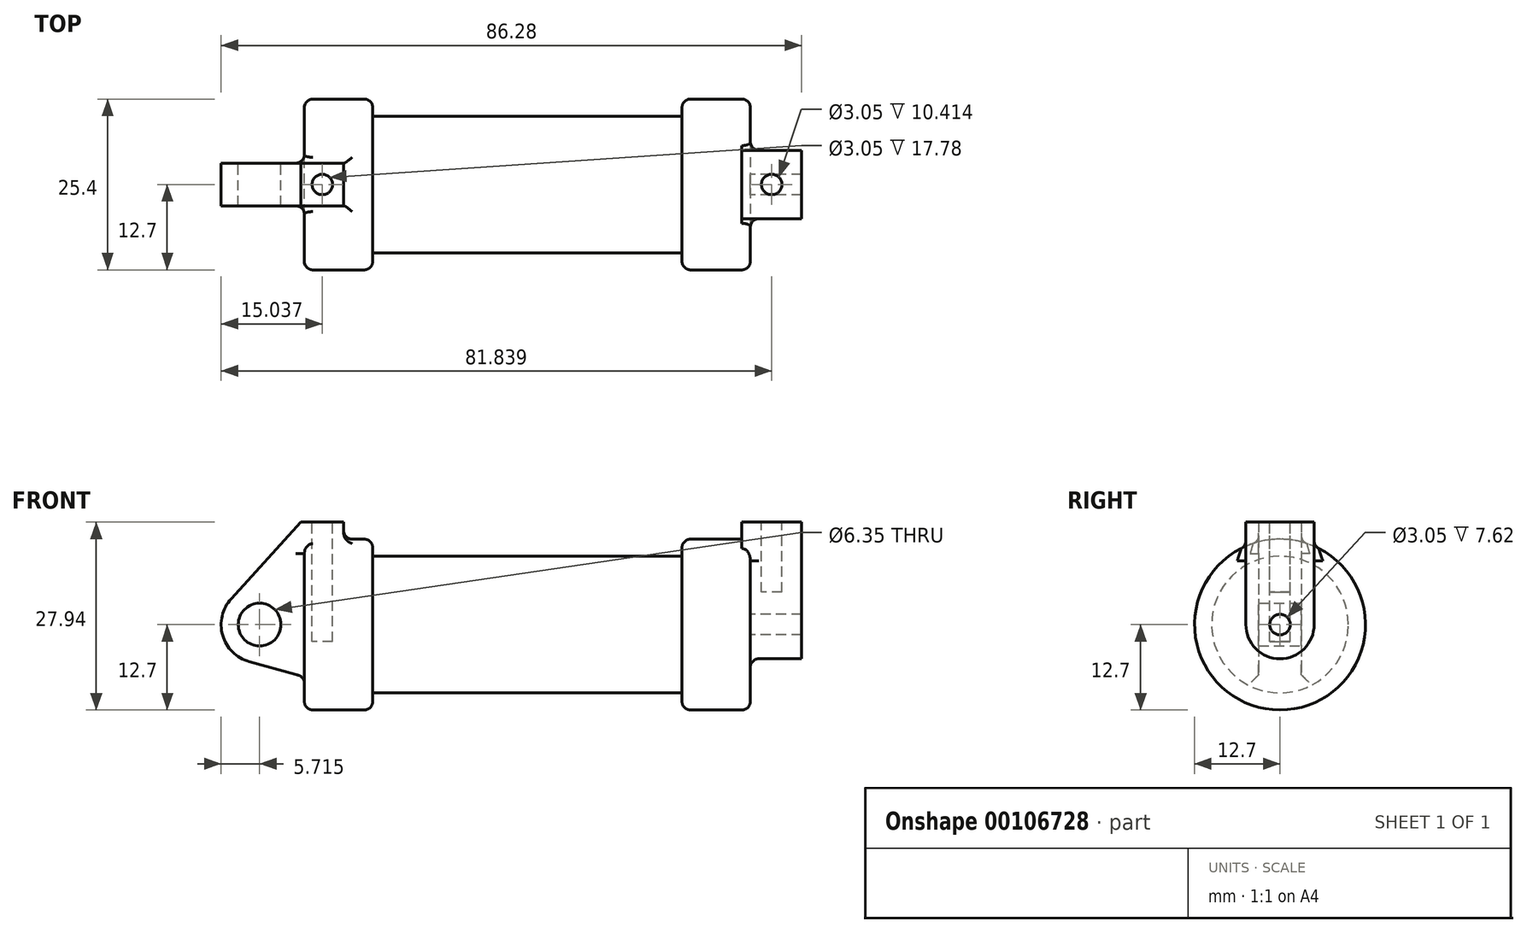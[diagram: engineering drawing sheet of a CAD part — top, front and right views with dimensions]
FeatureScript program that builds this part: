
annotation { "Feature Type Name" : "Feature", "Feature Type Description" : "" }
export const myFeature = defineFeature(function(context is Context, id is Id, definition is map)
    precondition{}
    {
        {
            var Q0;
            Q0=qCreatedBy(makeId("Front.planeOp"),FACE);
            var sketch = newSketch(context, id + "F0", { "sketchPlane" : qUnion([Q0])});
            skLineSegment(sketch, "E0", {"start": v(0, 0) * mm, "end": v(0, 12.7) * mm});
            skLineSegment(sketch, "E1", {"start": v(0, 12.7) * mm, "end": v(10.16, 12.7) * mm});
            skLineSegment(sketch, "E2", {"start": v(10.16, 12.7) * mm, "end": v(10.16, 10.16) * mm});
            skLineSegment(sketch, "E3", {"start": v(10.16, 10.16) * mm, "end": v(56.13, 10.16) * mm});
            skLineSegment(sketch, "E4", {"start": v(56.13, 10.16) * mm, "end": v(56.13, 12.7) * mm});
            skLineSegment(sketch, "E5", {"start": v(56.13, 12.7) * mm, "end": v(66.3, 12.7) * mm});
            skLineSegment(sketch, "E6", {"start": v(66.3, 12.7) * mm, "end": v(66.3, 0) * mm});
            skLineSegment(sketch, "E7", {"start": v(66.3, 0) * mm, "end": v(0, 0) * mm});
            skLineSegment(sketch, "E8", {"start": v(5.84, 15.24) * mm, "end": v(-0.5, 15.24) * mm});
            skLineSegment(sketch, "E9", {"start": v(-0.5, 15.24) * mm, "end": v(-10.88, 3.85) * mm});
            skLineSegment(sketch, "E10", {"start": v(0, 0) * mm, "end": v(-6.65, 0) * mm});
            skCircle(sketch, "E11", {"center": v(-6.65, 0) * mm, "radius": 5.72 * mm});
            skCircle(sketch, "E12", {"center": v(-6.65, 0) * mm, "radius": 3.18 * mm});
            skLineSegment(sketch, "E13", {"start": v(5.84, 15.24) * mm, "end": v(5.84, -9.4) * mm});
            skLineSegment(sketch, "E14", {"start": v(5.84, -9.4) * mm, "end": v(-8.18, -5.5) * mm});
            skSolve(sketch);
        }
        {
            var Q0;
            {var subQ0=sQuery(id+"F0.wireOp",EDGE,"E0");Q0=makeQuery(id+"F0.imprint","IMPRINT",FACE,{"disambiguationData":[TD([[makeQuery(id+"F0.imprint","IMPRINT",EDGE,{"derivedFrom":subQ0}),-1.0]])]});}
            var Q1;
            {var subQ0=sQuery(id+"F0.wireOp",EDGE,"E2");Q1=makeQuery(id+"F0.imprint","IMPRINT",FACE,{"disambiguationData":[TD([[makeQuery(id+"F0.imprint","IMPRINT",EDGE,{"derivedFrom":subQ0}),-1.0]])]});}
            var Q2;
            Q2=sQuery(id+"F0.wireOp",EDGE,"E7");
            revolve(context, id + "F1", {"entities" : qUnion([Q0, Q1]), "axis" : qUnion([Q2]), "revolveType" : RevolveType.FULL});
        }
        {
            var Q0;
            {var subQ3=sQuery(id+"F0.wireOp",EDGE,"E0");Q0=makeQuery(id+"F0.imprint","IMPRINT",FACE,{"disambiguationData":[TD([[makeQuery(id+"F0.imprint","IMPRINT",EDGE,{"derivedFrom":subQ3}),1.0]])]});}
            var Q1;
            {var subQ4=sQuery(id+"F0.wireOp",EDGE,"E12");Q1=makeQuery(id+"F0.imprint","IMPRINT",FACE,{"disambiguationData":[TD([[makeQuery(id+"F0.imprint","IMPRINT",EDGE,{"derivedFrom":subQ4}),-1.0]])]});}
            var Q2;
            {var subQ0=sQuery(id+"F0.wireOp",EDGE,"E14");Q2=makeQuery(id+"F0.imprint","IMPRINT",FACE,{"disambiguationData":[TD([[makeQuery(id+"F0.imprint","IMPRINT",EDGE,{"derivedFrom":subQ0}),-1.0]])]});}
            var Q3;
            {var subQ0=sQuery(id+"F0.wireOp",EDGE,"E0");Q3=makeQuery(id+"F0.imprint","IMPRINT",FACE,{"disambiguationData":[TD([[makeQuery(id+"F0.imprint","IMPRINT",EDGE,{"derivedFrom":subQ0}),-1.0]])]});}
            extrude(context, id + "F2", {"entities" : qUnion([Q0, Q1, Q2, Q3]), "operationType" : NewBodyOperationType.ADD, "endBound" : BoundingType.SYMMETRIC, "depth" : 6.35 * mm});
        }
        {
            var Q0;
            Q0=makeQuery(id+"F1.opRevolve","SWEPT_FACE",FACE,{"disambiguationData":[OSD([sQuery(id+"F0.wireOp",EDGE,"E6")])]});
            var sketch = newSketch(context, id + "F3", { "sketchPlane" : qUnion([Q0])});
            skCircle(sketch, "E15", {"center": v(0, 0) * mm, "radius": 1.52 * mm});
            skCircle(sketch, "E16", {"center": v(0, 0) * mm, "radius": 5.08 * mm});
            skLineSegment(sketch, "E17", {"start": v(5.08, 0) * mm, "end": v(5.08, 15.24) * mm});
            skLineSegment(sketch, "E18", {"start": v(-5.08, 0) * mm, "end": v(-5.08, 15.24) * mm});
            skLineSegment(sketch, "E19", {"start": v(-5.08, 15.24) * mm, "end": v(5.08, 15.24) * mm});
            skSolve(sketch);
        }
        {
            var Q0;
            {var subQ0=sQuery(id+"F3.wireOp",EDGE,"E19");Q0=makeQuery(id+"F3.imprint","IMPRINT",FACE,{"disambiguationData":[TD([[makeQuery(id+"F3.imprint","IMPRINT",EDGE,{"derivedFrom":subQ0}),-1.0]])]});}
            var Q1;
            {var subQ0=sQuery(id+"F3.wireOp",EDGE,"E17");var subQ1=sQuery(id+"F3.wireOp",EDGE,"E16");var subQ2=makeQuery(id+"F3.imprint","INTERSECT",VERTEX,{"derivedFrom":[subQ1,subQ0]});Q1=makeQuery(id+"F3.imprint","IMPRINT",FACE,{"disambiguationData":[TD([[makeQuery(id+"F3.imprint","IMPRINT",EDGE,{"disambiguationData":[TD([[subQ2,-1.0]])],"derivedFrom":subQ1}),-1.0]])]});}
            var Q2;
            Q2=makeQuery(id+"F3.imprint","IMPRINT",FACE,{"disambiguationData":[TD([[makeQuery(id+"F3.imprint","IMPRINT",EDGE,{"derivedFrom":sQuery(id+"F3.wireOp",EDGE,"E15")}),-1.0]])]});
            extrude(context, id + "F4", {"entities" : qUnion([Q0, Q1, Q2]), "operationType" : NewBodyOperationType.ADD, "depth" : 7.62 * mm});
        }
        {
            var Q0;
            Q0=makeQuery(id+"F4.opExtrude","CAP_FACE",FACE,{"disambiguationData":[OSD([sQuery(id+"F3.wireOp",EDGE,"E15"),sQuery(id+"F3.wireOp",EDGE,"E16"),sQuery(id+"F3.wireOp",EDGE,"E17"),sQuery(id+"F3.wireOp",EDGE,"E18"),sQuery(id+"F3.wireOp",EDGE,"E19")])],"isStart":true});
            extrude(context, id + "F5", {"entities" : qUnion([Q0]), "operationType" : NewBodyOperationType.ADD, "depth" : 1.27 * mm});
        }
        {
            var Q0;
            Q0=makeQuery(id+"F4.boolean.opBoolean","SPLIT",FACE,{"disambiguationData":[TD([makeQuery(id+"F4.opExtrude","SWEPT_FACE",FACE,{"disambiguationData":[OSD([sQuery(id+"F3.wireOp",EDGE,"E15")])]})])],"derivedFrom":makeQuery(id+"F1.opRevolve","SWEPT_FACE",FACE,{"disambiguationData":[OSD([sQuery(id+"F0.wireOp",EDGE,"E6")])]})});
            var Q1;
            Q1=makeQuery(id+"F1.opRevolve","SWEPT_FACE",FACE,{"disambiguationData":[OSD([sQuery(id+"F0.wireOp",EDGE,"E2")])]});
            extrude(context, id + "F6", {"entities" : qUnion([Q0]), "operationType" : NewBodyOperationType.ADD, "endBound" : BoundingType.UP_TO_SURFACE, "oppositeDirection" : true, "endBoundEntityFace" : qUnion([Q1]), "depth" : 25.4 * mm});
        }
        {
            var Q0;
            {var subQ0=sQuery(id+"F3.wireOp",EDGE,"E19");Q0=makeQuery(id+"F5.boolean.opBoolean","MERGE",FACE,{"derivedFrom":[makeQuery(id+"F4.opExtrude","SWEPT_FACE",FACE,{"disambiguationData":[OSD([subQ0])]}),makeQuery(id+"F5.opExtrude","SWEPT_FACE",FACE,{"disambiguationData":[OSD([subQ0])]})]});}
            var sketch = newSketch(context, id + "F7", { "sketchPlane" : qUnion([Q0])});
            skCircle(sketch, "E20", {"center": v(69.47, 0) * mm, "radius": 1.52 * mm});
            skPoint(sketch, "E20.centerSnap0", {"position": v(69.47, -5.08) * mm});
            skPoint(sketch, "E20.centerSnap1", {"position": v(65.02, 0) * mm});
            skSolve(sketch);
        }
        {
            var Q0;
            Q0=makeQuery(id+"F7.imprint","IMPRINT",FACE,{"disambiguationData":[TD([[makeQuery(id+"F7.imprint","IMPRINT",EDGE,{"derivedFrom":sQuery(id+"F7.wireOp",EDGE,"E20")}),1.0]])]});
            extrude(context, id + "F8", {"entities" : qUnion([Q0]), "operationType" : NewBodyOperationType.REMOVE, "oppositeDirection" : true, "depth" : 10.4 * mm});
        }
        {
            var Q0;
            Q0=makeQuery(id+"F2.opExtrude","SWEPT_FACE",FACE,{"disambiguationData":[OSD([sQuery(id+"F0.wireOp",EDGE,"E8")])]});
            var sketch = newSketch(context, id + "F9", { "sketchPlane" : qUnion([Q0])});
            skCircle(sketch, "E21", {"center": v(2.67, 0) * mm, "radius": 1.52 * mm});
            skPoint(sketch, "E21.centerSnap0", {"position": v(2.67, -3.18) * mm});
            skPoint(sketch, "E21.centerSnap1", {"position": v(-0.5, 0) * mm});
            skSolve(sketch);
        }
        {
            var Q0;
            Q0=makeQuery(id+"F9.imprint","IMPRINT",FACE,{"disambiguationData":[TD([[makeQuery(id+"F9.imprint","IMPRINT",EDGE,{"derivedFrom":sQuery(id+"F9.wireOp",EDGE,"E21")}),1.0]])]});
            extrude(context, id + "F10", {"entities" : qUnion([Q0]), "operationType" : NewBodyOperationType.REMOVE, "oppositeDirection" : true, "depth" : 17.78 * mm});
        }
        {
            var Q0;
            Q0=makeQuery(id+"F4.boolean.opBoolean","SPLIT",EDGE,{"disambiguationData":[OD(1.0)],"derivedFrom":makeQuery(id+"F1.opRevolve","SWEPT_EDGE",EDGE,{"disambiguationData":[OSD([sQuery(id+"F0.wireOp",EDGE,"E5"),sQuery(id+"F0.wireOp",EDGE,"E6")])]})});
            fillet(context, id + "F11", {"entities" : qUnion([Q0]), "radius" : 1.27 * mm, "tangentPropagation" : true, "allowEdgeOverflow" : false});
        }
        {
            var Q0;
            Q0=makeQuery(id+"F1.opRevolve","SWEPT_EDGE",EDGE,{"disambiguationData":[OSD([sQuery(id+"F0.wireOp",EDGE,"E1"),sQuery(id+"F0.wireOp",EDGE,"E2")])]});
            fillet(context, id + "F12", {"entities" : qUnion([Q0]), "radius" : 1.27 * mm, "tangentPropagation" : true, "allowEdgeOverflow" : false});
        }
        {
            var Q0;
            Q0=makeQuery(id+"F1.opRevolve","SWEPT_EDGE",EDGE,{"disambiguationData":[OSD([sQuery(id+"F0.wireOp",EDGE,"E0"),sQuery(id+"F0.wireOp",EDGE,"E1")])]});
            fillet(context, id + "F13", {"entities" : qUnion([Q0]), "radius" : 1.27 * mm, "tangentPropagation" : true, "allowEdgeOverflow" : false});
        }
        {
            var Q0;
            Q0=makeQuery(id+"F1.opRevolve","SWEPT_EDGE",EDGE,{"disambiguationData":[OSD([sQuery(id+"F0.wireOp",EDGE,"E4"),sQuery(id+"F0.wireOp",EDGE,"E5")])]});
            fillet(context, id + "F14", {"entities" : qUnion([Q0]), "radius" : 1.27 * mm, "tangentPropagation" : true, "allowEdgeOverflow" : false});
        }
        {
            var Q0;
            {var subQ0=sQuery(id+"F3.wireOp",EDGE,"E18");var subQ1=sQuery(id+"F3.wireOp",EDGE,"E16");Q0=makeQuery(id+"F4.boolean.opBoolean","SPLIT",EDGE,{"disambiguationData":[TD([makeQuery(id+"F4.opExtrude","SWEPT_FACE",FACE,{"disambiguationData":[OSD([subQ1])]})])],"derivedFrom":makeQuery(id+"F4.opExtrude","CAP_EDGE",EDGE,{"disambiguationData":[OSD([subQ0])],"isStart":true})});}
            var Q1;
            Q1=makeQuery(id+"F4.opExtrude","CAP_EDGE",EDGE,{"disambiguationData":[OSD([sQuery(id+"F3.wireOp",EDGE,"E16")])],"isStart":true});
            var Q2;
            {var subQ0=sQuery(id+"F3.wireOp",EDGE,"E17");var subQ1=sQuery(id+"F3.wireOp",EDGE,"E16");Q2=makeQuery(id+"F4.boolean.opBoolean","SPLIT",EDGE,{"disambiguationData":[TD([makeQuery(id+"F4.opExtrude","SWEPT_FACE",FACE,{"disambiguationData":[OSD([subQ1])]})])],"derivedFrom":makeQuery(id+"F4.opExtrude","CAP_EDGE",EDGE,{"disambiguationData":[OSD([subQ0])],"isStart":true})});}
            var Q3;
            Q3=makeQuery(id+"F5.opExtrude","CAP_EDGE",EDGE,{"disambiguationData":[OSD([sQuery(id+"F0.wireOp",EDGE,"E5"),sQuery(id+"F0.wireOp",EDGE,"E6")])],"isStart":false});
            fillet(context, id + "F15", {"entities" : qUnion([Q0, Q1, Q2, Q3]), "radius" : 1.27 * mm, "tangentPropagation" : true, "allowEdgeOverflow" : false});
        }
        {
            var Q0;
            Q0=makeQuery(id+"F2.boolean.opBoolean","INTERSECT",EDGE,{"derivedFrom":[makeQuery(id+"F1.opRevolve","SWEPT_FACE",FACE,{"disambiguationData":[OSD([sQuery(id+"F0.wireOp",EDGE,"E0")])]}),makeQuery(id+"F2.opExtrude","CAP_FACE",FACE,{"disambiguationData":[OSD([sQuery(id+"F0.wireOp",EDGE,"E8"),sQuery(id+"F0.wireOp",EDGE,"E9"),sQuery(id+"F0.wireOp",EDGE,"E11"),sQuery(id+"F0.wireOp",EDGE,"E12"),sQuery(id+"F0.wireOp",EDGE,"E13"),sQuery(id+"F0.wireOp",EDGE,"E14")])],"isStart":false})]});
            var Q1;
            Q1=makeQuery(id+"F2.boolean.opBoolean","INTERSECT",EDGE,{"derivedFrom":[makeQuery(id+"F1.opRevolve","SWEPT_FACE",FACE,{"disambiguationData":[OSD([sQuery(id+"F0.wireOp",EDGE,"E0")])]}),makeQuery(id+"F2.opExtrude","SWEPT_FACE",FACE,{"disambiguationData":[OSD([sQuery(id+"F0.wireOp",EDGE,"E14")])]})]});
            var Q2;
            Q2=makeQuery(id+"F2.boolean.opBoolean","INTERSECT",EDGE,{"derivedFrom":[makeQuery(id+"F1.opRevolve","SWEPT_FACE",FACE,{"disambiguationData":[OSD([sQuery(id+"F0.wireOp",EDGE,"E0")])]}),makeQuery(id+"F2.opExtrude","CAP_FACE",FACE,{"disambiguationData":[OSD([sQuery(id+"F0.wireOp",EDGE,"E8"),sQuery(id+"F0.wireOp",EDGE,"E9"),sQuery(id+"F0.wireOp",EDGE,"E11"),sQuery(id+"F0.wireOp",EDGE,"E12"),sQuery(id+"F0.wireOp",EDGE,"E13"),sQuery(id+"F0.wireOp",EDGE,"E14")])],"isStart":true})]});
            fillet(context, id + "F16", {"entities" : qUnion([Q0, Q1, Q2]), "radius" : 1.27 * mm, "tangentPropagation" : true, "allowEdgeOverflow" : false});
        }
        {
            var Q0;
            Q0=makeQuery(id+"F2.boolean.opBoolean","INTERSECT",EDGE,{"derivedFrom":[makeQuery(id+"F1.opRevolve","SWEPT_FACE",FACE,{"disambiguationData":[OSD([sQuery(id+"F0.wireOp",EDGE,"E1")])]}),makeQuery(id+"F2.opExtrude","SWEPT_FACE",FACE,{"disambiguationData":[OSD([sQuery(id+"F0.wireOp",EDGE,"E13")])]})]});
            fillet(context, id + "F17", {"entities" : qUnion([Q0]), "radius" : 1.27 * mm, "tangentPropagation" : true, "allowEdgeOverflow" : false});
        }
    });
